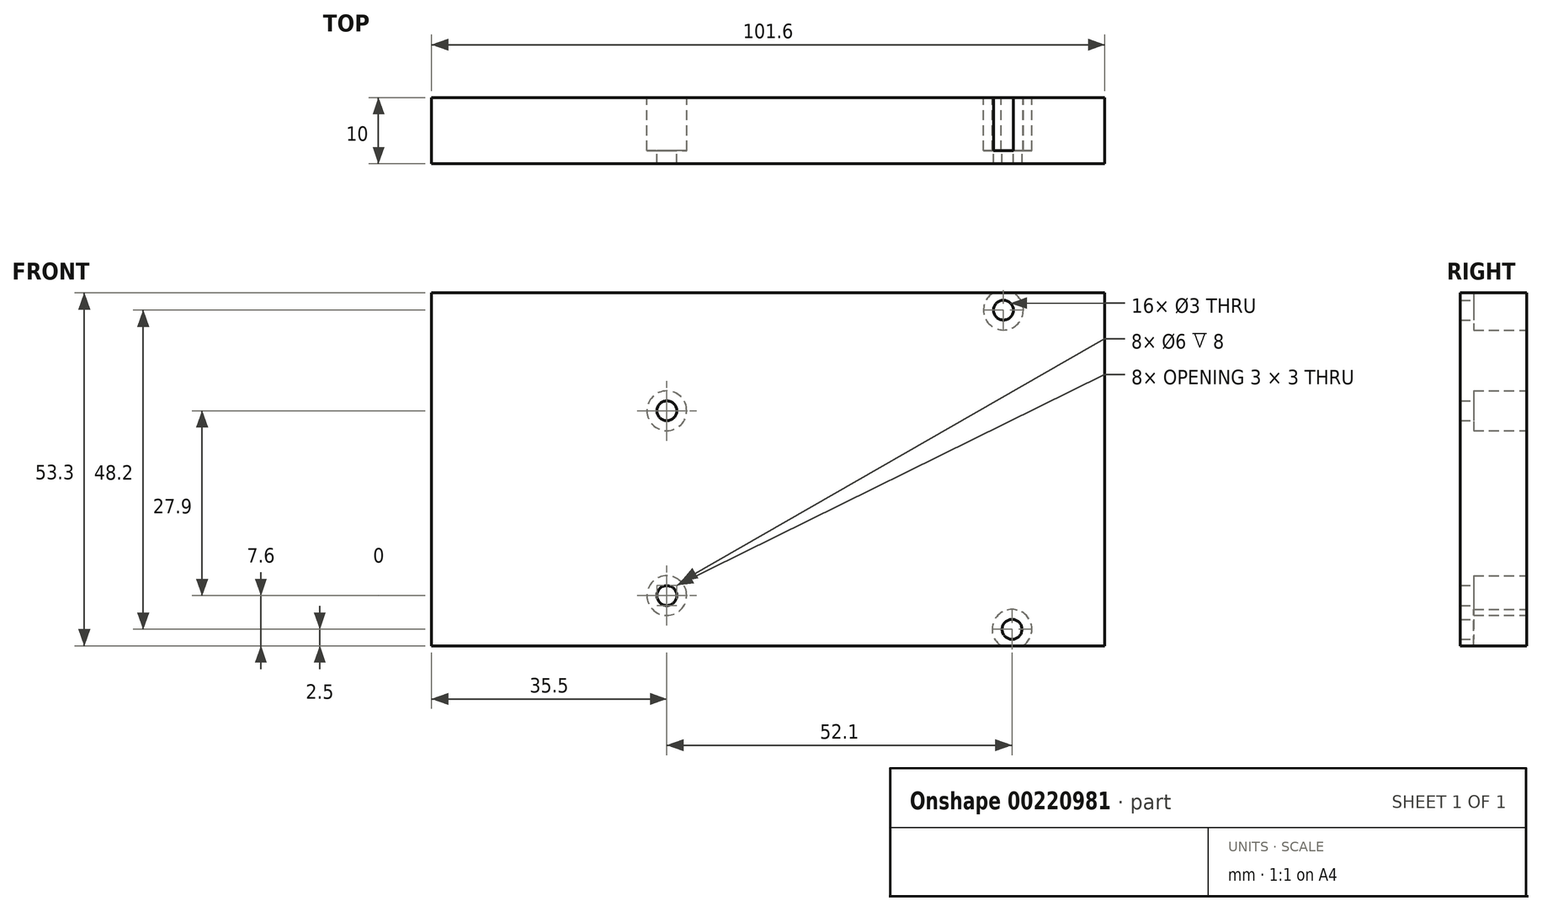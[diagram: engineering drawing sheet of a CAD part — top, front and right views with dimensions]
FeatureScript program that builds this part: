
annotation { "Feature Type Name" : "Feature", "Feature Type Description" : "" }
export const myFeature = defineFeature(function(context is Context, id is Id, definition is map)
    precondition{}
    {
        {
            var Q0;
            Q0=qCreatedBy(makeId("Front.planeOp"),FACE);
            var sketch = newSketch(context, id + "F0", { "sketchPlane" : qUnion([Q0])});
            skLineSegment(sketch, "E0.bottom", {"start": v(-50.8, 26.65) * mm, "end": v(50.8, 26.65) * mm});
            skLineSegment(sketch, "E0.top", {"start": v(-50.8, -26.65) * mm, "end": v(50.8, -26.65) * mm});
            skLineSegment(sketch, "E0.left", {"start": v(-50.8, 26.65) * mm, "end": v(-50.8, -26.65) * mm});
            skLineSegment(sketch, "E0.right", {"start": v(50.8, 26.65) * mm, "end": v(50.8, -26.65) * mm});
            skPoint(sketch, "E0.middle", {"position": v(0, 0) * mm});
            skLineSegment(sketch, "E1", {"start": v(50.8, -26.65) * mm, "end": v(50.8, -24.15) * mm});
            skLineSegment(sketch, "E2", {"start": v(50.8, -24.15) * mm, "end": v(36.8, -24.15) * mm});
            skLineSegment(sketch, "E3", {"start": v(36.8, -24.15) * mm, "end": v(35.5, -24.15) * mm});
            skLineSegment(sketch, "E4", {"start": v(35.5, -24.15) * mm, "end": v(35.5, 24.05) * mm});
            skLineSegment(sketch, "E5", {"start": v(35.5, 24.05) * mm, "end": v(-15.3, 24.05) * mm});
            skLineSegment(sketch, "E6", {"start": v(-15.3, 24.05) * mm, "end": v(-15.3, 8.85) * mm});
            skLineSegment(sketch, "E7", {"start": v(-15.3, 24.05) * mm, "end": v(-39.4, 24.05) * mm});
            skLineSegment(sketch, "E8", {"start": v(-15.3, 8.85) * mm, "end": v(-15.3, -19.05) * mm});
            skCircle(sketch, "E9", {"center": v(36.8, -24.15) * mm, "radius": 1.5 * mm});
            skCircle(sketch, "E10", {"center": v(35.5, 24.05) * mm, "radius": 1.5 * mm});
            skCircle(sketch, "E11", {"center": v(-15.3, 8.85) * mm, "radius": 1.5 * mm});
            skCircle(sketch, "E12", {"center": v(-15.3, -19.05) * mm, "radius": 1.5 * mm});
            skSolve(sketch);
        }
        {
            var Q0;
            Q0 = qSketchRegion(id + "F0", true);
            extrude(context, id + "F1", {"entities" : qUnion([Q0]), "depth" : 10 * mm});
        }
        {
            var Q0;
            Q0=makeQuery(id+"F1.opExtrude","CAP_FACE",FACE,{"disambiguationData":[OSD([sQuery(id+"F0.wireOp",EDGE,"E0.bottom"),sQuery(id+"F0.wireOp",EDGE,"E0.top"),sQuery(id+"F0.wireOp",EDGE,"E0.left"),sQuery(id+"F0.wireOp",EDGE,"E0.right"),sQuery(id+"F0.wireOp",EDGE,"E1"),sQuery(id+"F0.wireOp",EDGE,"E9"),sQuery(id+"F0.wireOp",EDGE,"E10"),sQuery(id+"F0.wireOp",EDGE,"E11"),sQuery(id+"F0.wireOp",EDGE,"E12")])],"isStart":true});
            var sketch = newSketch(context, id + "F2", { "sketchPlane" : qUnion([Q0])});
            skCircle(sketch, "E13", {"center": v(-35.5, 24.05) * mm, "radius": 3 * mm});
            skCircle(sketch, "E14", {"center": v(-36.8, -24.15) * mm, "radius": 3 * mm});
            skCircle(sketch, "E15", {"center": v(15.3, -19.05) * mm, "radius": 3 * mm});
            skCircle(sketch, "E16", {"center": v(15.3, 8.85) * mm, "radius": 3 * mm});
            skSolve(sketch);
        }
        {
            var Q0;
            Q0 = qSketchRegion(id + "F2", true);
            extrude(context, id + "F3", {"entities" : qUnion([Q0]), "operationType" : NewBodyOperationType.REMOVE, "oppositeDirection" : true, "depth" : 8 * mm});
        }
    });
